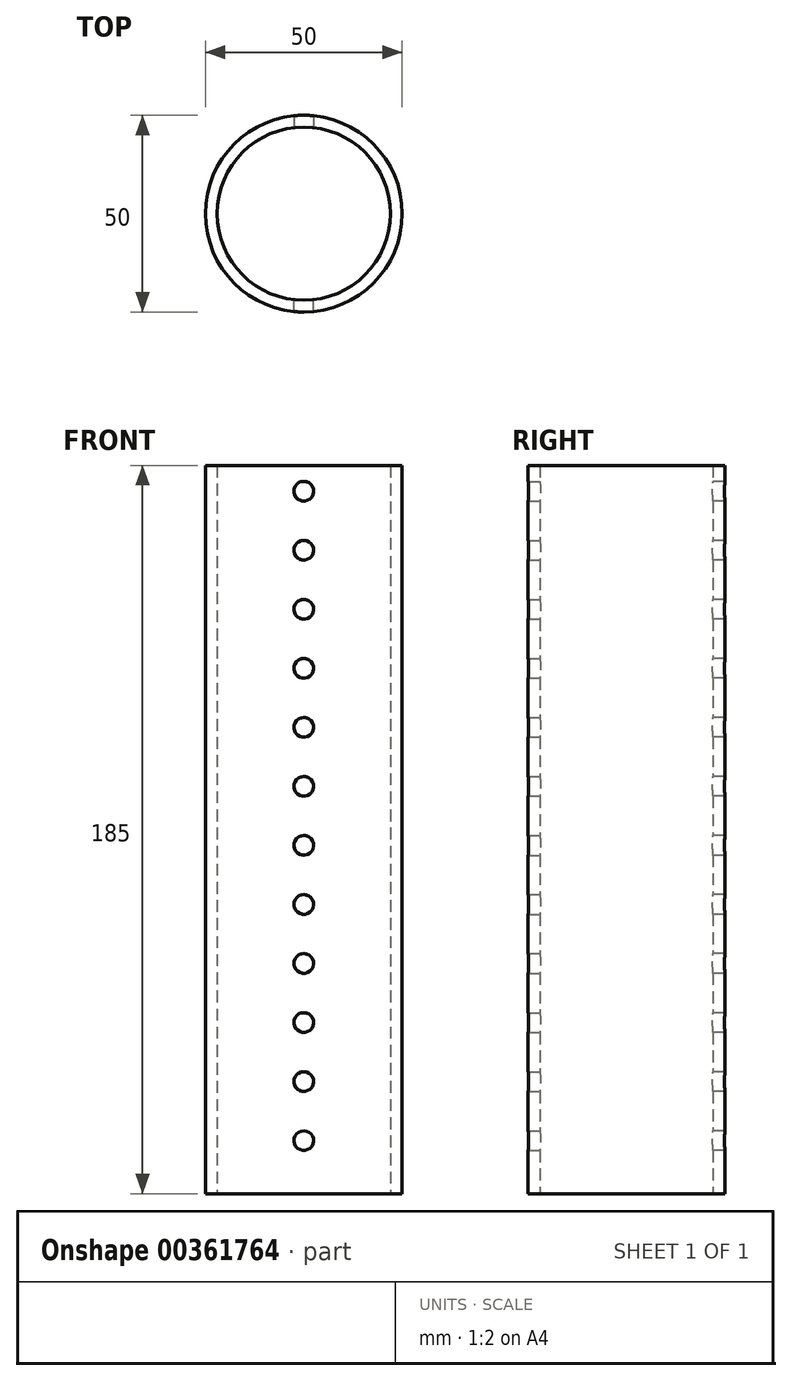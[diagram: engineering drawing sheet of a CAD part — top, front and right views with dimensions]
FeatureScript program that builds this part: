
annotation { "Feature Type Name" : "Feature", "Feature Type Description" : "" }
export const myFeature = defineFeature(function(context is Context, id is Id, definition is map)
    precondition{}
    {
        {
            var Q0;
            Q0=qCreatedBy(makeId("Top.planeOp"),FACE);
            var sketch = newSketch(context, id + "F0", { "sketchPlane" : qUnion([Q0])});
            skCircle(sketch, "E0", {"center": v(0, 0) * mm, "radius": 22 * mm});
            skCircle(sketch, "E1", {"center": v(0, 0) * mm, "radius": 25 * mm});
            skSolve(sketch);
        }
        {
            var Q0;
            Q0=makeQuery(id+"F0.imprint","IMPRINT",FACE,{"disambiguationData":[TD([[makeQuery(id+"F0.imprint","IMPRINT",EDGE,{"derivedFrom":sQuery(id+"F0.wireOp",EDGE,"E0")}),-1.0]])]});
            extrude(context, id + "F1", {"entities" : qUnion([Q0]), "depth" : 185 * mm});
        }
        {
            var Q0;
            Q0=qCreatedBy(makeId("Front.planeOp"),FACE);
            var sketch = newSketch(context, id + "F2", { "sketchPlane" : qUnion([Q0])});
            skPoint(sketch, "E2", {"position": v(0, 193.48) * mm});
            skPoint(sketch, "E3.0.1.0", {"position": v(0, 178.48) * mm});
            skPoint(sketch, "E3.0.2.0", {"position": v(0, 163.48) * mm});
            skPoint(sketch, "E3.0.3.0", {"position": v(0, 148.48) * mm});
            skPoint(sketch, "E3.0.4.0", {"position": v(0, 133.48) * mm});
            skPoint(sketch, "E3.0.5.0", {"position": v(0, 118.48) * mm});
            skPoint(sketch, "E3.0.6.0", {"position": v(0, 103.48) * mm});
            skPoint(sketch, "E3.0.7.0", {"position": v(0, 88.48) * mm});
            skPoint(sketch, "E3.0.8.0", {"position": v(0, 73.48) * mm});
            skPoint(sketch, "E3.0.9.0", {"position": v(0, 58.48) * mm});
            skPoint(sketch, "E3.0.10.0", {"position": v(0, 43.48) * mm});
            skPoint(sketch, "E3.0.11.0", {"position": v(0, 28.48) * mm});
            skPoint(sketch, "E3.0.12.0", {"position": v(0, 13.48) * mm});
            skLineSegment(sketch, "E3.direction1", {"start": v(0, 193.48) * mm, "end": v(-16, 193.48) * mm, "construction": true});
            skLineSegment(sketch, "E3.direction2", {"start": v(0, 193.48) * mm, "end": v(0, 178.48) * mm, "construction": true});
            skLineSegment(sketch, "E4", {"start": v(0, 0) * mm, "end": v(0, 193.48) * mm});
            skSolve(sketch);
        }
        {
            var Q0;
            Q0=sQuery(id+"F2.wireOp",VERTEX,"E3.0.1.0");
            var Q1;
            Q1=sQuery(id+"F2.wireOp",VERTEX,"E3.0.2.0");
            var Q2;
            Q2=sQuery(id+"F2.wireOp",VERTEX,"E3.0.3.0");
            var Q3;
            Q3=sQuery(id+"F2.wireOp",VERTEX,"E3.0.4.0");
            var Q4;
            Q4=sQuery(id+"F2.wireOp",VERTEX,"E3.0.5.0");
            var Q5;
            Q5=sQuery(id+"F2.wireOp",VERTEX,"E3.0.6.0");
            var Q6;
            Q6=sQuery(id+"F2.wireOp",VERTEX,"E3.0.7.0");
            var Q7;
            Q7=sQuery(id+"F2.wireOp",VERTEX,"E3.0.8.0");
            var Q8;
            Q8=sQuery(id+"F2.wireOp",VERTEX,"E3.0.9.0");
            var Q9;
            Q9=sQuery(id+"F2.wireOp",VERTEX,"E3.0.10.0");
            var Q10;
            Q10=sQuery(id+"F2.wireOp",VERTEX,"E3.0.11.0");
            var Q11;
            Q11=sQuery(id+"F2.wireOp",VERTEX,"E3.0.12.0");
            var Q12;
            Q12=makeQuery(id+"F1.opExtrude","SWEPT_BODY",BODY,{"disambiguationData":[OSD([sQuery(id+"F0.wireOp",EDGE,"E0"),sQuery(id+"F0.wireOp",EDGE,"E1")])]});
            hole(context, id + "F3", {"style" : HoleStyle.SIMPLE, "endStyle" : HoleEndStyle.THROUGH, "holeDiameter" : 5 * mm, "isTappedThrough" : true, "tappedDepth" : 12 * mm, "tapClearance" : 3, "startFromSketch" : true, "locations" : qUnion([Q0, Q1, Q2, Q3, Q4, Q5, Q6, Q7, Q8, Q9, Q10, Q11]), "scope" : qUnion([Q12])});
        }
        {
            var Q0;
            Q0=sQuery(id+"F2.wireOp",VERTEX,"E3.0.1.0");
            var Q1;
            Q1=sQuery(id+"F2.wireOp",VERTEX,"E3.0.2.0");
            var Q2;
            Q2=sQuery(id+"F2.wireOp",VERTEX,"E3.0.3.0");
            var Q3;
            Q3=sQuery(id+"F2.wireOp",VERTEX,"E3.0.4.0");
            var Q4;
            Q4=sQuery(id+"F2.wireOp",VERTEX,"E3.0.5.0");
            var Q5;
            Q5=sQuery(id+"F2.wireOp",VERTEX,"E3.0.6.0");
            var Q6;
            Q6=sQuery(id+"F2.wireOp",VERTEX,"E3.0.7.0");
            var Q7;
            Q7=sQuery(id+"F2.wireOp",VERTEX,"E3.0.8.0");
            var Q8;
            Q8=sQuery(id+"F2.wireOp",VERTEX,"E3.0.9.0");
            var Q9;
            Q9=sQuery(id+"F2.wireOp",VERTEX,"E3.0.10.0");
            var Q10;
            Q10=sQuery(id+"F2.wireOp",VERTEX,"E3.0.11.0");
            var Q11;
            Q11=sQuery(id+"F2.wireOp",VERTEX,"E3.0.12.0");
            var Q12;
            Q12=makeQuery(id+"F1.opExtrude","SWEPT_BODY",BODY,{"disambiguationData":[OSD([sQuery(id+"F0.wireOp",EDGE,"E0"),sQuery(id+"F0.wireOp",EDGE,"E1")])]});
            hole(context, id + "F4", {"style" : HoleStyle.SIMPLE, "endStyle" : HoleEndStyle.THROUGH, "oppositeDirection" : true, "holeDiameter" : 5 * mm, "isTappedThrough" : true, "tappedDepth" : 12 * mm, "tapClearance" : 3, "startFromSketch" : true, "locations" : qUnion([Q0, Q1, Q2, Q3, Q4, Q5, Q6, Q7, Q8, Q9, Q10, Q11]), "scope" : qUnion([Q12])});
        }
    });
